# Revit family: Recycle Space Front
name_source: partatom
category: Furniture
revit_build: Autodesk Revit 2018 (Build: 20181011_1500(x64)
units: mm (PartAtom-declared; Revit-internal decimal feet)

## family parameters
Always vertical = No
Cut with Voids When Loaded = No
OmniClass Number = 23.40.20.00
OmniClass Title = General Furniture and Specialties
Room Calculation Point = No
Shared = No
Work Plane-Based = No

## types (9) — shared parameters
Bin Gap Front = 20 mm  [stored 0.0656168 ft]
Bin Hole Doors = 222 mm
Bisley_Depth = 470 mm  [stored 1.54199 ft]
Category = Furniture
Compliance Standards Certification = BS EN 14073 2004 Part 2 & 3, BS EN 14074, BS 4875 1998 Part 7 level 4 & Part 8, BS 476 Part 7 1987 Class 2Y
Description = -
DurationUnit = Years
ExpectedLife = > 10
Manufacturer = Bisley
ManufacturerName = Bisley
Model = ModelReference
Range = LateralFile
Revision = V1
Routine Maintenance = We recommend you clean your unit with warm water and a mild detergent solution. A damp cloth can be used to remove dust particles.
Tollerance = 2 mm  [stored 0.00656168 ft]
Type Comments = -
URL = www.bisley.com
Uniclass2015Code = Pr_40_50_07_70
Uniclass2015Title = Shelves and storage units
Uniclass2015Version = v1.5
WarrantyDurationUnit = Years
WarrantyGuarantorParts = 10
WarrantyStartDate = Date of Delivery

## per-type parameters (varying)
| type | Bin opener | Bisley_Height | Bisley_Width | Carcass Size | Left Door | ModelReference | Right Door | Size | Unit Height | bins height |
| FRCY3B08D30 | Bin Front top bit : 800 wide | 997 mm | 800 mm  [stored 2.62467 ft] | Carcasses : 08C30 | Left Door 3 : 08D30 Left Door | FRYC3B08D33 | Right Door 4 : 08D30 Right Door | 800mm x 1111mm x 470mm | 1001 mm | 328 mm |
| FRCY3B08D33 | Bin Front top bit : 800 wide | 1111 mm  [stored 3.64501 ft] | 800 mm  [stored 2.62467 ft] | Carcasses : 08C33 | Left Door 3 : 08D33 Left Door | FRYC3B08D33 | Right Door 4 : 08D33 Right Door | 800mm x 1111mm x 470mm | 1115 mm | 933 mm |
| FRCY3B08D34 | Bin Front top bit : 800 wide | 1149 mm  [stored 3.76969 ft] | 800 mm  [stored 2.62467 ft] | Carcasses : 08C34 | Left Door 3 : 08D34 Left Door | FRYC3B08D34 | Right Door 4 : 08D34 Right Door | 800mm x 1149mm x 470mm | 1153 mm | 933 mm |
| FRCY3B09D30 | Bin Front top bit : 900 wide | 997 mm | 900 mm  [stored 2.95276 ft] | Carcasses : 09C30 | Left Door 3 : 09D30 Left Door | FRYC3B09D30 | Right Door 4 : 09D30 Right Door | 900mm x 997mm x 470mm | 1001 mm | 328 mm |
| FRCY3B09D34 | Bin Front top bit : 900 wide | 1149 mm  [stored 3.76969 ft] | 900 mm  [stored 2.95276 ft] | Carcasses : 09C34 | Left Door 3 : 09D34 Left Door | FRYC3B09D30 | Right Door 4 : 09D34 Right Door | 900mm x 997mm x 470mm | 1153 mm | 328 mm |
| FRCY3B09D33 | Bin Front top bit : 900 wide | 1111 mm  [stored 3.64501 ft] | 900 mm  [stored 2.95276 ft] | Carcasses : 09C33 | Left Door 3 : 09D33 Left Door | FRYC3B09D33 | Right Door 4 : 09D33 Right Door | 900mm x 1111mm x 470mm | 1115 mm | 328 mm |
| FRCY3B10D30 | Bin Front top bit : 1000 wide | 997 mm | 1000 mm  [stored 3.28084 ft] | Carcasses : 10C30 | Left Door 3 : 10D30 Left Door | FRCY3B10D30 | Right Door 4 : 10D30 Right Door | 1000mm x 997mm x 470mm | 1001 mm | 328 mm |
| FRCY3B10D33 | Bin Front top bit : 1000 wide | 1111 mm  [stored 3.64501 ft] | 1000 mm  [stored 3.28084 ft] | Carcasses : 10C33 | Left Door 3 : 10D33 Left Door | FRCY3B10D33 | Right Door 4 : 10D33 Right Door | 1000mm x 1111mm x 470mm | 1115 mm | 328 mm |
| FRCY3B10D34 | Bin Front top bit : 1000 wide | 1149 mm  [stored 3.76969 ft] | 1000 mm  [stored 3.28084 ft] | Carcasses : 10C34 | Left Door 3 : 10D34 Left Door | FRCY3B10D34 | Right Door 4 : 10D34 Right Door | 1000mm x 1149mm x 470mm | 1153 mm | 328 mm |

note: [stored X ft] marks values corroborated as IEEE doubles in the binary element streams (Revit-internal decimal feet)

## geometry (parser evidence)
native form markers: Sweep x106
no freeform markers — native parametric forms only
